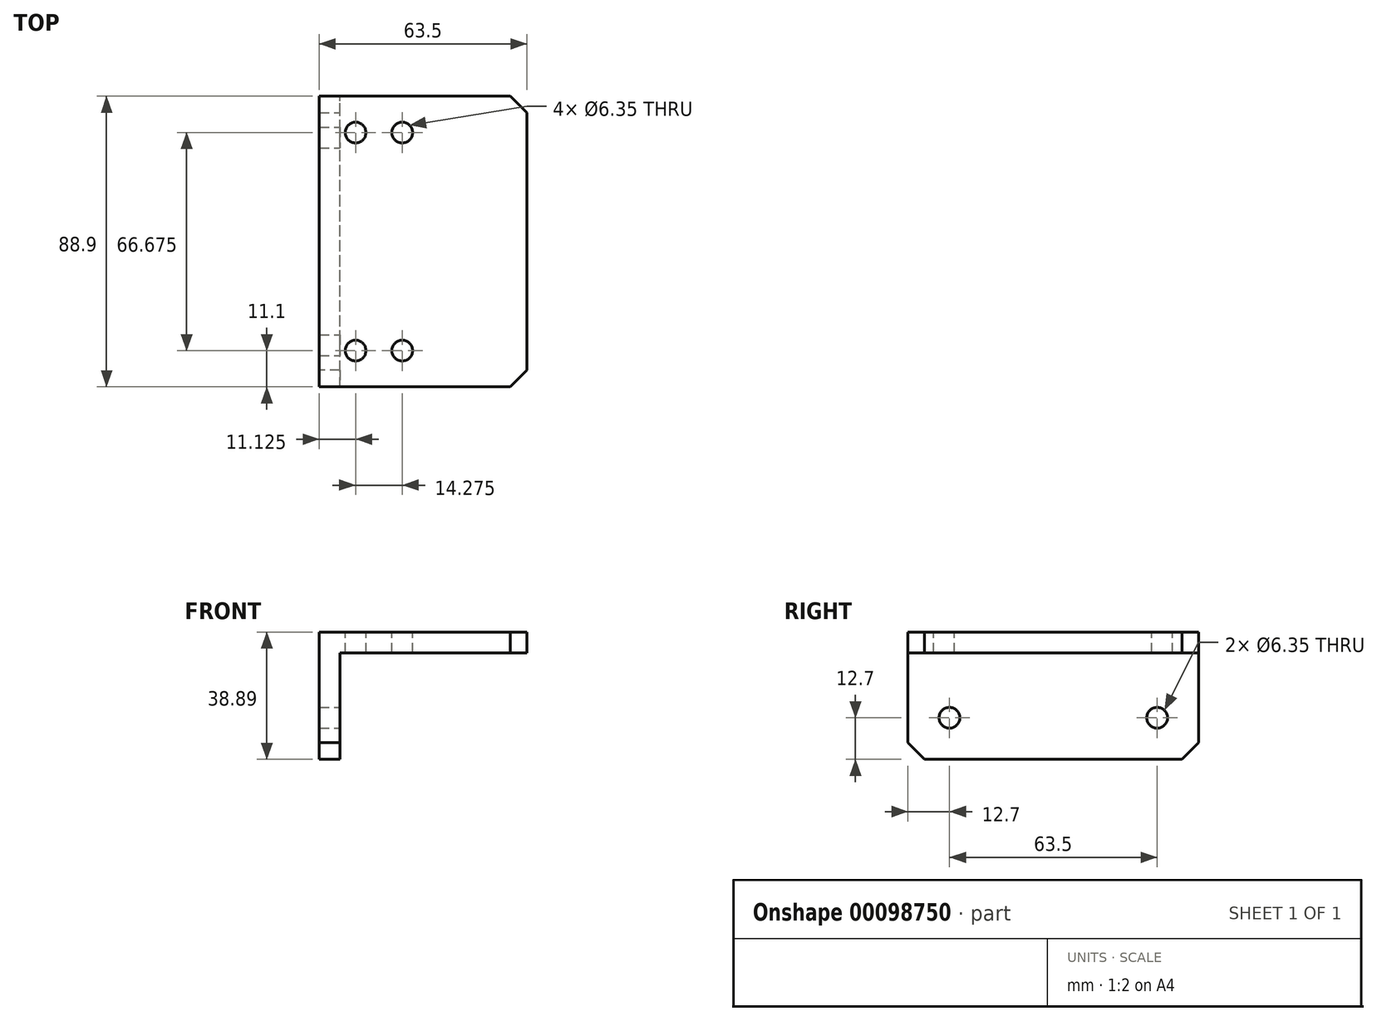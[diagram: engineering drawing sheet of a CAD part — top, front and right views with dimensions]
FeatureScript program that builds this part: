
annotation { "Feature Type Name" : "Feature", "Feature Type Description" : "" }
export const myFeature = defineFeature(function(context is Context, id is Id, definition is map)
    precondition{}
    {
        {
            var Q0;
            Q0=qCreatedBy(makeId("Front.planeOp"),FACE);
            var sketch = newSketch(context, id + "F0", { "sketchPlane" : qUnion([Q0])});
            skLineSegment(sketch, "E0", {"start": v(0, 0) * mm, "end": v(0, 38.89) * mm});
            skLineSegment(sketch, "E1", {"start": v(0, 38.89) * mm, "end": v(63.5, 38.89) * mm});
            skLineSegment(sketch, "E2", {"start": v(63.5, 38.89) * mm, "end": v(63.5, 32.54) * mm});
            skLineSegment(sketch, "E3", {"start": v(63.5, 32.54) * mm, "end": v(6.35, 32.54) * mm});
            skLineSegment(sketch, "E4", {"start": v(6.35, 32.54) * mm, "end": v(6.35, 0) * mm});
            skLineSegment(sketch, "E5", {"start": v(6.35, 0) * mm, "end": v(0, 0) * mm});
            skSolve(sketch);
        }
        {
            var Q0;
            Q0=makeQuery(id+"F0.imprint","IMPRINT",FACE,{"disambiguationData":[TD([[makeQuery(id+"F0.imprint","IMPRINT",EDGE,{"derivedFrom":sQuery(id+"F0.wireOp",EDGE,"E0")}),-1.0]])]});
            extrude(context, id + "F1", {"entities" : qUnion([Q0]), "depth" : 88.9 * mm});
        }
        {
            var Q0;
            Q0=makeQuery(id+"F1.opExtrude","SWEPT_FACE",FACE,{"disambiguationData":[OSD([sQuery(id+"F0.wireOp",EDGE,"E4")])]});
            var sketch = newSketch(context, id + "F2", { "sketchPlane" : qUnion([Q0])});
            skPoint(sketch, "E6", {"position": v(-76.2, 12.7) * mm});
            skPoint(sketch, "E7", {"position": v(-12.7, 12.7) * mm});
            skSolve(sketch);
        }
        {
            var Q0;
            Q0=sQuery(id+"F2.wireOp",VERTEX,"E6");
            var Q1;
            Q1=sQuery(id+"F2.wireOp",VERTEX,"E7");
            var Q2;
            Q2=makeQuery(id+"F1.opExtrude","SWEPT_BODY",BODY,{"disambiguationData":[OSD([sQuery(id+"F0.wireOp",EDGE,"E0"),sQuery(id+"F0.wireOp",EDGE,"E1"),sQuery(id+"F0.wireOp",EDGE,"E2"),sQuery(id+"F0.wireOp",EDGE,"E3"),sQuery(id+"F0.wireOp",EDGE,"E4"),sQuery(id+"F0.wireOp",EDGE,"E5")])]});
            hole(context, id + "F3", {"style" : HoleStyle.SIMPLE, "endStyle" : HoleEndStyle.THROUGH, "holeDiameter" : 6.35 * mm, "locations" : qUnion([Q0, Q1]), "scope" : qUnion([Q2]), "isTappedThrough" : true});
        }
        {
            var Q0;
            Q0=makeQuery(id+"F1.opExtrude","CAP_EDGE",EDGE,{"disambiguationData":[OSD([sQuery(id+"F0.wireOp",EDGE,"E5")])],"isStart":false});
            var Q1;
            Q1=makeQuery(id+"F1.opExtrude","CAP_EDGE",EDGE,{"disambiguationData":[OSD([sQuery(id+"F0.wireOp",EDGE,"E2")])],"isStart":false});
            var Q2;
            Q2=makeQuery(id+"F1.opExtrude","CAP_EDGE",EDGE,{"disambiguationData":[OSD([sQuery(id+"F0.wireOp",EDGE,"E2")])],"isStart":true});
            var Q3;
            Q3=makeQuery(id+"F1.opExtrude","CAP_EDGE",EDGE,{"disambiguationData":[OSD([sQuery(id+"F0.wireOp",EDGE,"E5")])],"isStart":true});
            chamfer(context, id + "F4", {"entities" : qUnion([Q0, Q1, Q2, Q3]), "width" : 5.08 * mm, "tangentPropagation" : true});
        }
        {
            var Q0;
            Q0=makeQuery(id+"F1.opExtrude","SWEPT_FACE",FACE,{"disambiguationData":[OSD([sQuery(id+"F0.wireOp",EDGE,"E1")])]});
            var sketch = newSketch(context, id + "F5", { "sketchPlane" : qUnion([Q0])});
            skPoint(sketch, "E8", {"position": v(11.13, -11.13) * mm});
            skPoint(sketch, "E9", {"position": v(25.4, -11.13) * mm});
            skPoint(sketch, "E10", {"position": v(11.13, -77.8) * mm});
            skPoint(sketch, "E11", {"position": v(25.4, -77.8) * mm});
            skSolve(sketch);
        }
        {
            var Q0;
            Q0=sQuery(id+"F5.wireOp",VERTEX,"E9");
            var Q1;
            Q1=sQuery(id+"F5.wireOp",VERTEX,"E8");
            var Q2;
            Q2=sQuery(id+"F5.wireOp",VERTEX,"E10");
            var Q3;
            Q3=sQuery(id+"F5.wireOp",VERTEX,"E11");
            var Q4;
            Q4=makeQuery(id+"F1.opExtrude","SWEPT_BODY",BODY,{"disambiguationData":[OSD([sQuery(id+"F0.wireOp",EDGE,"E0"),sQuery(id+"F0.wireOp",EDGE,"E1"),sQuery(id+"F0.wireOp",EDGE,"E2"),sQuery(id+"F0.wireOp",EDGE,"E3"),sQuery(id+"F0.wireOp",EDGE,"E4"),sQuery(id+"F0.wireOp",EDGE,"E5")])]});
            hole(context, id + "F6", {"style" : HoleStyle.SIMPLE, "endStyle" : HoleEndStyle.THROUGH, "holeDiameter" : 6.35 * mm, "locations" : qUnion([Q0, Q1, Q2, Q3]), "scope" : qUnion([Q4]), "isTappedThrough" : true});
        }
    });
